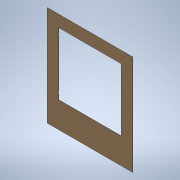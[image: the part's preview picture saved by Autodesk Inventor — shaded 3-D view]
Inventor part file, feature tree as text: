
AUTODESK INVENTOR PART (.ipt)
format: ipt  version: 2022 (Build 260153000, 153)  size: 159,232 bytes
history: native  units: mm
features: sketch x4, extrude x3, other x1, fillet x1, hole x1
ambient origin geometry x8: Origin, YZ Plane, XZ Plane, XY Plane, X Axis, Y Axis, Z Axis, Center Point
bodies: Body1 (feature_tree)
feature tree (10):
  other  "Sólido1"
  extrude  "Extrusão1"  Depth=700.0mm
  extrude  "Extrusão2"  Depth=80.0mm
  fillet  "Arredondamento1"  Radius=80.0mm
  hole  "Furo1"  [1 undecoded]
  extrude  "Extrusão3"  Depth=2.0mm
  sketch  "Esboço1"  dims[d0=600.0mm d1=700.0mm]
  sketch  "Esboço2"  dims[d2=3.0mm d3=0.0mm d4=80.0mm d5=80.0mm]
  sketch  "Esboço3"  dims[d6=80.0mm d7=180.0mm]
  sketch  "Esboço4"  dims[d8=10.0mm d9=0.0mm d10=2.0mm d11=2.0mm d12=6.0mm d13=4.0mm d14=2.0mm d15=90.0deg d16=8.0mm d17=20.594885mm d19=3.0mm d20=18.0mm d21=3.0mm d22=18.0mm d23=10.0mm d24=0.0mm]
note: 1 required parameter value undecoded (feature->parameter linkage not recoverable at this tier; creation-order binding heuristic only, values carry confidence <= 0.55)
